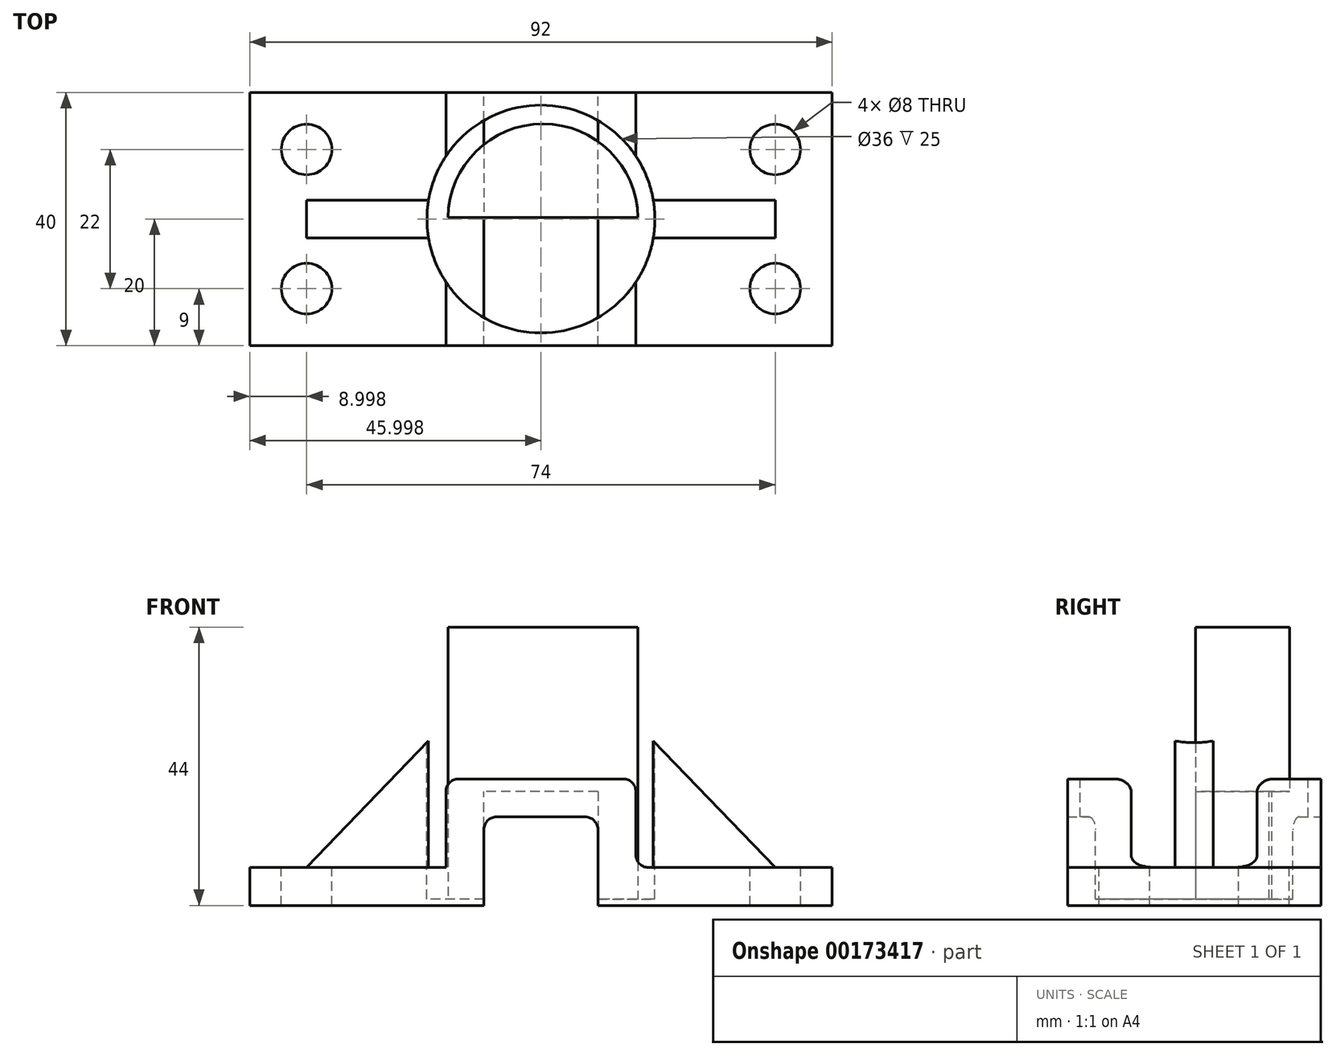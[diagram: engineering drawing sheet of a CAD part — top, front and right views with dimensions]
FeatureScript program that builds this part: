
annotation { "Feature Type Name" : "Feature", "Feature Type Description" : "" }
export const myFeature = defineFeature(function(context is Context, id is Id, definition is map)
    precondition{}
    {
        {
            var Q0;
            Q0=qCreatedBy(makeId("Front.planeOp"),FACE);
            var sketch = newSketch(context, id + "F0", { "sketchPlane" : qUnion([Q0])});
            skLineSegment(sketch, "E0", {"start": v(45.69, 0) * mm, "end": v(8.69, 0) * mm});
            skLineSegment(sketch, "E1", {"start": v(8.69, 0) * mm, "end": v(8.69, 12) * mm});
            skLineSegment(sketch, "E2", {"start": v(6.69, 14) * mm, "end": v(-7.31, 14) * mm});
            skLineSegment(sketch, "E3", {"start": v(-9.31, 12) * mm, "end": v(-9.31, 0) * mm});
            skLineSegment(sketch, "E4", {"start": v(-9.31, 0) * mm, "end": v(-46.31, 0) * mm});
            skLineSegment(sketch, "E5.0", {"start": v(-15.31, 6) * mm, "end": v(-46.31, 6) * mm});
            skLineSegment(sketch, "E5.1", {"start": v(45.69, 6) * mm, "end": v(16.69, 6) * mm});
            skLineSegment(sketch, "E5.2", {"start": v(14.69, 8) * mm, "end": v(14.69, 18) * mm});
            skLineSegment(sketch, "E5.3", {"start": v(12.69, 20) * mm, "end": v(-13.31, 20) * mm});
            skLineSegment(sketch, "E5.4", {"start": v(-15.31, 18) * mm, "end": v(-15.31, 6) * mm});
            skLineSegment(sketch, "E6", {"start": v(-46.31, 6) * mm, "end": v(-46.31, 0) * mm});
            skLineSegment(sketch, "E7", {"start": v(45.69, 6) * mm, "end": v(45.69, 0) * mm});
            skPoint(sketch, "E8.visualSharp", {"position": v(-15.31, 20) * mm});
            skArc(sketch, "E8.filletArc", {"start": v(-13.31, 20) * mm, "mid": v(-14.73, 19.41) * mm, "end": v(-15.31, 18) * mm});
            skPoint(sketch, "E9.visualSharp", {"position": v(-9.31, 14) * mm});
            skArc(sketch, "E9.filletArc", {"start": v(-7.31, 14) * mm, "mid": v(-8.73, 13.41) * mm, "end": v(-9.31, 12) * mm});
            skPoint(sketch, "E10.visualSharp", {"position": v(14.69, 6) * mm});
            skArc(sketch, "E10.filletArc", {"start": v(14.69, 8) * mm, "mid": v(15.27, 6.59) * mm, "end": v(16.69, 6) * mm});
            skPoint(sketch, "E11.visualSharp", {"position": v(14.69, 20) * mm});
            skArc(sketch, "E11.filletArc", {"start": v(14.69, 18) * mm, "mid": v(14.1, 19.41) * mm, "end": v(12.69, 20) * mm});
            skPoint(sketch, "E12.visualSharp", {"position": v(8.69, 14) * mm});
            skArc(sketch, "E12.filletArc", {"start": v(8.69, 12) * mm, "mid": v(8.1, 13.41) * mm, "end": v(6.69, 14) * mm});
            skSolve(sketch);
        }
        {
            var Q0;
            Q0=makeQuery(id+"F0.imprint","IMPRINT",FACE,{"disambiguationData":[TD([[makeQuery(id+"F0.imprint","IMPRINT",EDGE,{"derivedFrom":sQuery(id+"F0.wireOp",EDGE,"E0")}),-1.0]])]});
            extrude(context, id + "F1", {"entities" : qUnion([Q0]), "depth" : 40 * mm});
        }
        {
            var Q0;
            Q0=makeQuery(id+"F1.opExtrude","SWEPT_FACE",FACE,{"disambiguationData":[OSD([sQuery(id+"F0.wireOp",EDGE,"E5.0")])]});
            var sketch = newSketch(context, id + "F14", { "sketchPlane" : qUnion([Q0])});
            skCircle(sketch, "E13", {"center": v(-37.31, -9) * mm, "radius": 4 * mm});
            skCircle(sketch, "E14", {"center": v(-37.31, -31) * mm, "radius": 4 * mm});
            skSolve(sketch);
        }
        {
            var Q0;
            Q0=makeQuery(id+"F14.imprint","IMPRINT",FACE,{"disambiguationData":[TD([[makeQuery(id+"F14.imprint","IMPRINT",EDGE,{"derivedFrom":sQuery(id+"F14.wireOp",EDGE,"E14")}),1.0]])]});
            var Q1;
            Q1=makeQuery(id+"F14.imprint","IMPRINT",FACE,{"disambiguationData":[TD([[makeQuery(id+"F14.imprint","IMPRINT",EDGE,{"derivedFrom":sQuery(id+"F14.wireOp",EDGE,"E13")}),1.0]])]});
            extrude(context, id + "F2", {"entities" : qUnion([Q0, Q1]), "operationType" : NewBodyOperationType.REMOVE, "oppositeDirection" : true, "depth" : 6 * mm});
        }
        {
            var Q0;
            Q0=makeQuery(id+"F1.opExtrude","SWEPT_FACE",FACE,{"disambiguationData":[OSD([sQuery(id+"F0.wireOp",EDGE,"E5.0")])]});
            var sketch = newSketch(context, id + "F3", { "sketchPlane" : qUnion([Q0])});
            skCircle(sketch, "E15", {"center": v(36.69, -9) * mm, "radius": 4 * mm});
            skCircle(sketch, "E16", {"center": v(36.69, -31) * mm, "radius": 4 * mm});
            skSolve(sketch);
        }
        {
            var Q0;
            Q0=makeQuery(id+"F3.imprint","IMPRINT",FACE,{"disambiguationData":[TD([[makeQuery(id+"F3.imprint","IMPRINT",EDGE,{"derivedFrom":sQuery(id+"F3.wireOp",EDGE,"E16")}),1.0]])]});
            var Q1;
            Q1=makeQuery(id+"F3.imprint","IMPRINT",FACE,{"disambiguationData":[TD([[makeQuery(id+"F3.imprint","IMPRINT",EDGE,{"derivedFrom":sQuery(id+"F3.wireOp",EDGE,"E15")}),1.0]])]});
            extrude(context, id + "F15", {"entities" : qUnion([Q0, Q1]), "operationType" : NewBodyOperationType.REMOVE, "oppositeDirection" : true, "depth" : 6 * mm});
        }
        {
            var Q0;
            Q0=makeQuery(id+"F1.opExtrude","SWEPT_FACE",FACE,{"disambiguationData":[OSD([sQuery(id+"F0.wireOp",EDGE,"E5.3")])]});
            var sketch = newSketch(context, id + "F4", { "sketchPlane" : qUnion([Q0])});
            skCircle(sketch, "E17", {"center": v(-0.31, -20) * mm, "radius": 18 * mm});
            skPoint(sketch, "E18.trimOffspring.end.orphan", {"position": v(-13.31, 0) * mm});
            skPoint(sketch, "E19.start.orphan", {"position": v(12.69, -40) * mm});
            skSolve(sketch);
        }
        {
            var Q0;
            {var subQ0=sQuery(id+"F4.wireOp",EDGE,"E17");var subQ1=makeQuery(id+"F1.opExtrude","SWEPT_EDGE",EDGE,{"disambiguationData":[OSD([sQuery(id+"F0.wireOp",EDGE,"E5.3"),sQuery(id+"F0.wireOp",EDGE,"E8.filletArc")])]});var subQ2=makeQuery(id+"F4.imprint","INTERSECT",VERTEX,{"disambiguationData":[OD(0.0)],"derivedFrom":[subQ1,subQ0]});Q0=makeQuery(id+"F4.imprint","IMPRINT",FACE,{"disambiguationData":[TD([[makeQuery(id+"F4.imprint","IMPRINT",EDGE,{"disambiguationData":[TD([[subQ2,-1.0]])],"derivedFrom":subQ0}),1.0]])]});}
            var Q1;
            {var subQ0=sQuery(id+"F4.wireOp",EDGE,"E17");var subQ1=sQuery(id+"F0.wireOp",EDGE,"E5.3");var subQ2=makeQuery(id+"F1.opExtrude","SWEPT_EDGE",EDGE,{"disambiguationData":[OSD([subQ1,sQuery(id+"F0.wireOp",EDGE,"E8.filletArc")])]});var subQ3=makeQuery(id+"F4.imprint","INTERSECT",VERTEX,{"disambiguationData":[OD(0.0)],"derivedFrom":[subQ2,subQ0]});Q1=makeQuery(id+"F4.imprint","IMPRINT",FACE,{"disambiguationData":[TD([[makeQuery(id+"F4.imprint","IMPRINT",EDGE,{"disambiguationData":[TD([[subQ3,1.0]])],"derivedFrom":subQ0}),1.0]])]});}
            var Q2;
            {var subQ0=sQuery(id+"F4.wireOp",EDGE,"E17");var subQ1=makeQuery(id+"F1.opExtrude","SWEPT_EDGE",EDGE,{"disambiguationData":[OSD([sQuery(id+"F0.wireOp",EDGE,"E5.3"),sQuery(id+"F0.wireOp",EDGE,"E11.filletArc")])]});var subQ2=makeQuery(id+"F4.imprint","INTERSECT",VERTEX,{"disambiguationData":[OD(0.0)],"derivedFrom":[subQ1,subQ0]});Q2=makeQuery(id+"F4.imprint","IMPRINT",FACE,{"disambiguationData":[TD([[makeQuery(id+"F4.imprint","IMPRINT",EDGE,{"disambiguationData":[TD([[subQ2,1.0]])],"derivedFrom":subQ0}),1.0]])]});}
            extrude(context, id + "F16", {"entities" : qUnion([Q0, Q1, Q2]), "operationType" : NewBodyOperationType.ADD, "oppositeDirection" : true, "depth" : 14 * mm});
        }
        {
            var Q0;
            Q0=makeQuery(id+"F16.boolean.opBoolean","MERGE",FACE,{"derivedFrom":[makeQuery(id+"F1.opExtrude","SWEPT_FACE",FACE,{"disambiguationData":[OSD([sQuery(id+"F0.wireOp",EDGE,"E5.3")])]}),makeQuery(id+"F16.opExtrude","CAP_FACE",FACE,{"disambiguationData":[OSD([sQuery(id+"F4.wireOp",EDGE,"E17")])],"isStart":true})]});
            var sketch = newSketch(context, id + "F5", { "sketchPlane" : qUnion([Q0])});
            skCircle(sketch, "E20", {"center": v(-0.31, -20) * mm, "radius": 18 * mm});
            skPoint(sketch, "E21.start.orphan", {"position": v(12.69, -40) * mm});
            skPoint(sketch, "E22.trimOffspring.end.orphan", {"position": v(-13.31, 0) * mm});
            skSolve(sketch);
        }
        {
            var Q0;
            {var subQ0=sQuery(id+"F5.wireOp",EDGE,"E20");var subQ3=sQuery(id+"F0.wireOp",EDGE,"E11.filletArc");var subQ5=sQuery(id+"F0.wireOp",EDGE,"E5.3");var subQ7=sQuery(id+"F0.wireOp",EDGE,"E12.filletArc");var subQ8=sQuery(id+"F0.wireOp",EDGE,"E10.filletArc");var subQ9=sQuery(id+"F0.wireOp",EDGE,"E9.filletArc");var subQ10=sQuery(id+"F0.wireOp",EDGE,"E8.filletArc");var subQ11=sQuery(id+"F0.wireOp",EDGE,"E7");var subQ12=sQuery(id+"F0.wireOp",EDGE,"E6");var subQ13=sQuery(id+"F0.wireOp",EDGE,"E5.4");var subQ14=sQuery(id+"F0.wireOp",EDGE,"E5.2");var subQ15=sQuery(id+"F0.wireOp",EDGE,"E5.1");var subQ16=sQuery(id+"F0.wireOp",EDGE,"E5.0");var subQ17=sQuery(id+"F0.wireOp",EDGE,"E4");var subQ18=sQuery(id+"F0.wireOp",EDGE,"E3");var subQ19=sQuery(id+"F0.wireOp",EDGE,"E2");var subQ20=sQuery(id+"F0.wireOp",EDGE,"E1");var subQ21=sQuery(id+"F0.wireOp",EDGE,"E0");var subQ22=makeQuery(id+"F1.opExtrude","CAP_FACE",FACE,{"disambiguationData":[OSD([subQ21,subQ20,subQ19,subQ18,subQ17,subQ16,subQ15,subQ14,subQ5,subQ13,subQ12,subQ11,subQ10,subQ9,subQ8,subQ3,subQ7])],"isStart":true});var subQ24=makeQuery(id+"F1.opExtrude","SWEPT_EDGE",EDGE,{"disambiguationData":[OSD([subQ5,subQ3])]});var subQ25=makeQuery(id+"F5.imprint","INTERSECT",VERTEX,{"derivedFrom":[makeQuery(id+"F16.boolean.opBoolean","SPLIT",EDGE,{"disambiguationData":[TD([subQ22])],"derivedFrom":subQ24}),subQ0]});Q0=makeQuery(id+"F5.imprint","IMPRINT",FACE,{"disambiguationData":[TD([[makeQuery(id+"F5.imprint","IMPRINT",EDGE,{"disambiguationData":[TD([[subQ25,-1.0]])],"derivedFrom":subQ0}),1.0]])]});}
            extrude(context, id + "F6", {"entities" : qUnion([Q0]), "operationType" : NewBodyOperationType.ADD, "depth" : 6 * mm});
        }
        {
            var Q0;
            Q0=makeQuery(id+"F6.opExtrude","CAP_FACE",FACE,{"disambiguationData":[OSD([sQuery(id+"F5.wireOp",EDGE,"E20")])],"isStart":false});
            var sketch = newSketch(context, id + "F7", { "sketchPlane" : qUnion([Q0])});
            skLineSegment(sketch, "E23", {"start": v(0, 0) * mm, "end": v(0, -39.9) * mm});
            skLineSegment(sketch, "E24", {"start": v(17.69, -19.77) * mm, "end": v(-18.31, -19.77) * mm});
            skCircle(sketch, "E25", {"center": v(0, -19.95) * mm, "radius": 15 * mm});
            skCircle(sketch, "E26", {"center": v(0, -19.95) * mm, "radius": 10 * mm});
            skSolve(sketch);
        }
        {
            var Q0;
            {var subQ0=sQuery(id+"F7.wireOp",EDGE,"E26");var subQ1=sQuery(id+"F7.wireOp",EDGE,"E23");var subQ2=makeQuery(id+"F7.imprint","INTERSECT",VERTEX,{"disambiguationData":[OD(1.0)],"derivedFrom":[subQ1,subQ0]});Q0=makeQuery(id+"F7.imprint","IMPRINT",FACE,{"disambiguationData":[TD([[makeQuery(id+"F7.imprint","IMPRINT",EDGE,{"disambiguationData":[TD([[subQ2,-1.0]])],"derivedFrom":subQ1}),-1.0]])]});}
            var Q1;
            {var subQ0=sQuery(id+"F7.wireOp",EDGE,"E26");var subQ1=sQuery(id+"F7.wireOp",EDGE,"E23");var subQ2=makeQuery(id+"F7.imprint","INTERSECT",VERTEX,{"disambiguationData":[OD(1.0)],"derivedFrom":[subQ1,subQ0]});Q1=makeQuery(id+"F7.imprint","IMPRINT",FACE,{"disambiguationData":[TD([[makeQuery(id+"F7.imprint","IMPRINT",EDGE,{"disambiguationData":[TD([[subQ2,-1.0]])],"derivedFrom":subQ1}),1.0]])]});}
            var Q2;
            {var subQ0=sQuery(id+"F7.wireOp",EDGE,"E25");var subQ1=sQuery(id+"F7.wireOp",EDGE,"E23");var subQ2=makeQuery(id+"F7.imprint","INTERSECT",VERTEX,{"disambiguationData":[OD(0.0)],"derivedFrom":[subQ1,subQ0]});Q2=makeQuery(id+"F7.imprint","IMPRINT",FACE,{"disambiguationData":[TD([[makeQuery(id+"F7.imprint","IMPRINT",EDGE,{"disambiguationData":[TD([[subQ2,-1.0]])],"derivedFrom":subQ1}),1.0]])]});}
            var Q3;
            {var subQ0=sQuery(id+"F7.wireOp",EDGE,"E25");var subQ1=sQuery(id+"F7.wireOp",EDGE,"E23");var subQ2=makeQuery(id+"F7.imprint","INTERSECT",VERTEX,{"disambiguationData":[OD(0.0)],"derivedFrom":[subQ1,subQ0]});Q3=makeQuery(id+"F7.imprint","IMPRINT",FACE,{"disambiguationData":[TD([[makeQuery(id+"F7.imprint","IMPRINT",EDGE,{"disambiguationData":[TD([[subQ2,-1.0]])],"derivedFrom":subQ1}),-1.0]])]});}
            extrude(context, id + "F17", {"entities" : qUnion([Q0, Q1, Q2, Q3]), "operationType" : NewBodyOperationType.ADD, "depth" : 18 * mm});
        }
        {
            var Q0;
            Q0=makeQuery(id+"F17.boolean.opBoolean","SPLIT",FACE,{"disambiguationData":[TD([makeQuery(id+"F17.opExtrude","SWEPT_FACE",FACE,{"disambiguationData":[OSD([sQuery(id+"F7.wireOp",EDGE,"E26")])]})])],"derivedFrom":makeQuery(id+"F6.opExtrude","CAP_FACE",FACE,{"disambiguationData":[OSD([sQuery(id+"F5.wireOp",EDGE,"E20")])],"isStart":false})});
            extrude(context, id + "F18", {"entities" : qUnion([Q0]), "operationType" : NewBodyOperationType.REMOVE, "oppositeDirection" : true, "depth" : 25 * mm});
        }
        {
            var Q0;
            Q0=makeQuery(id+"F1.opExtrude","SWEPT_FACE",FACE,{"disambiguationData":[OSD([sQuery(id+"F0.wireOp",EDGE,"E5.1")])]});
            var sketch = newSketch(context, id + "F19", { "sketchPlane" : qUnion([Q0])});
            skLineSegment(sketch, "E27", {"start": v(36.69, -17) * mm, "end": v(36.69, -23) * mm});
            skLineSegment(sketch, "E28", {"start": v(36.69, -23) * mm, "end": v(17.44, -23) * mm});
            skPoint(sketch, "E28.endSnap0", {"position": v(17.44, -23) * mm});
            skLineSegment(sketch, "E29", {"start": v(36.69, -17) * mm, "end": v(17.44, -17) * mm});
            skSolve(sketch);
        }
        {
            var Q0;
            Q0=makeQuery(id+"F19.imprint","IMPRINT",FACE,{"disambiguationData":[TD([[makeQuery(id+"F19.imprint","IMPRINT",EDGE,{"derivedFrom":sQuery(id+"F19.wireOp",EDGE,"E27")}),-1.0]])]});
            extrude(context, id + "F8", {"entities" : qUnion([Q0]), "operationType" : NewBodyOperationType.ADD, "depth" : 20 * mm});
        }
        {
            var Q0;
            Q0=makeQuery(id+"F1.opExtrude","SWEPT_FACE",FACE,{"disambiguationData":[OSD([sQuery(id+"F0.wireOp",EDGE,"E5.1")])]});
            var sketch = newSketch(context, id + "F20", { "sketchPlane" : qUnion([Q0])});
            skLineSegment(sketch, "E30", {"start": v(-37.31, -17) * mm, "end": v(-37.31, -23) * mm});
            skLineSegment(sketch, "E31", {"start": v(-37.31, -23) * mm, "end": v(-18.06, -23) * mm});
            skLineSegment(sketch, "E32", {"start": v(-37.31, -17) * mm, "end": v(-18.06, -17) * mm});
            skLineSegment(sketch, "E33", {"start": v(-18.06, -17) * mm, "end": v(-37.31, -17) * mm});
            skArc(sketch, "E34", {"start": v(-18.06, -17) * mm, "mid": v(-18.31, -20) * mm, "end": v(-18.06, -23) * mm});
            skSolve(sketch);
        }
        {
            var Q0;
            Q0=makeQuery(id+"F20.imprint","IMPRINT",FACE,{"disambiguationData":[TD([[makeQuery(id+"F20.imprint","IMPRINT",EDGE,{"derivedFrom":sQuery(id+"F20.wireOp",EDGE,"E30")}),1.0]])]});
            extrude(context, id + "F9", {"entities" : qUnion([Q0]), "operationType" : NewBodyOperationType.ADD, "depth" : 20 * mm});
        }
        {
            var Q0;
            Q0=makeQuery(id+"F8.opExtrude","SWEPT_FACE",FACE,{"disambiguationData":[OSD([sQuery(id+"F19.wireOp",EDGE,"E28")])]});
            var sketch = newSketch(context, id + "F21", { "sketchPlane" : qUnion([Q0])});
            skLineSegment(sketch, "E35", {"start": v(36.69, 6) * mm, "end": v(17.44, 26) * mm});
            skSolve(sketch);
        }
        {
            var Q0;
            Q0 = qSketchRegion(id + "F21", true);
            var Q1;
            Q1=makeQuery(id+"F21.imprint","IMPRINT",FACE,{"disambiguationData":[TD([[makeQuery(id+"F21.imprint","IMPRINT",EDGE,{"derivedFrom":sQuery(id+"F21.wireOp",EDGE,"E35")}),-1.0]])]});
            extrude(context, id + "F10", {"entities" : qUnion([Q0, Q1]), "operationType" : NewBodyOperationType.REMOVE, "oppositeDirection" : true, "depth" : 6 * mm});
        }
        {
            var Q0;
            Q0=makeQuery(id+"F9.opExtrude","SWEPT_FACE",FACE,{"disambiguationData":[OSD([sQuery(id+"F20.wireOp",EDGE,"E31")])]});
            var sketch = newSketch(context, id + "F11", { "sketchPlane" : qUnion([Q0])});
            skLineSegment(sketch, "E36", {"start": v(-37.31, 6) * mm, "end": v(-18.06, 26) * mm});
            skSolve(sketch);
        }
        {
            var Q0;
            Q0 = qSketchRegion(id + "F11", true);
            var Q1;
            Q1=makeQuery(id+"F11.imprint","IMPRINT",FACE,{"disambiguationData":[TD([[makeQuery(id+"F11.imprint","IMPRINT",EDGE,{"derivedFrom":sQuery(id+"F11.wireOp",EDGE,"E36")}),1.0]])]});
            extrude(context, id + "F12", {"entities" : qUnion([Q0, Q1]), "operationType" : NewBodyOperationType.REMOVE, "oppositeDirection" : true, "depth" : 6 * mm});
        }
        {
            var Q0;
            Q0=makeQuery(id+"F18.boolean.opBoolean","SPLIT",FACE,{"disambiguationData":[OD(0.0)],"derivedFrom":makeQuery(id+"F16.opExtrude","CAP_FACE",FACE,{"disambiguationData":[OSD([sQuery(id+"F4.wireOp",EDGE,"E17")])],"isStart":false})});
            var Q1;
            Q1=makeQuery(id+"F18.boolean.opBoolean","SPLIT",FACE,{"disambiguationData":[OD(1.0)],"derivedFrom":makeQuery(id+"F16.opExtrude","CAP_FACE",FACE,{"disambiguationData":[OSD([sQuery(id+"F4.wireOp",EDGE,"E17")])],"isStart":false})});
            extrude(context, id + "F13", {"entities" : qUnion([Q0, Q1]), "operationType" : NewBodyOperationType.REMOVE, "oppositeDirection" : true, "depth" : 12 * mm});
        }
    });
